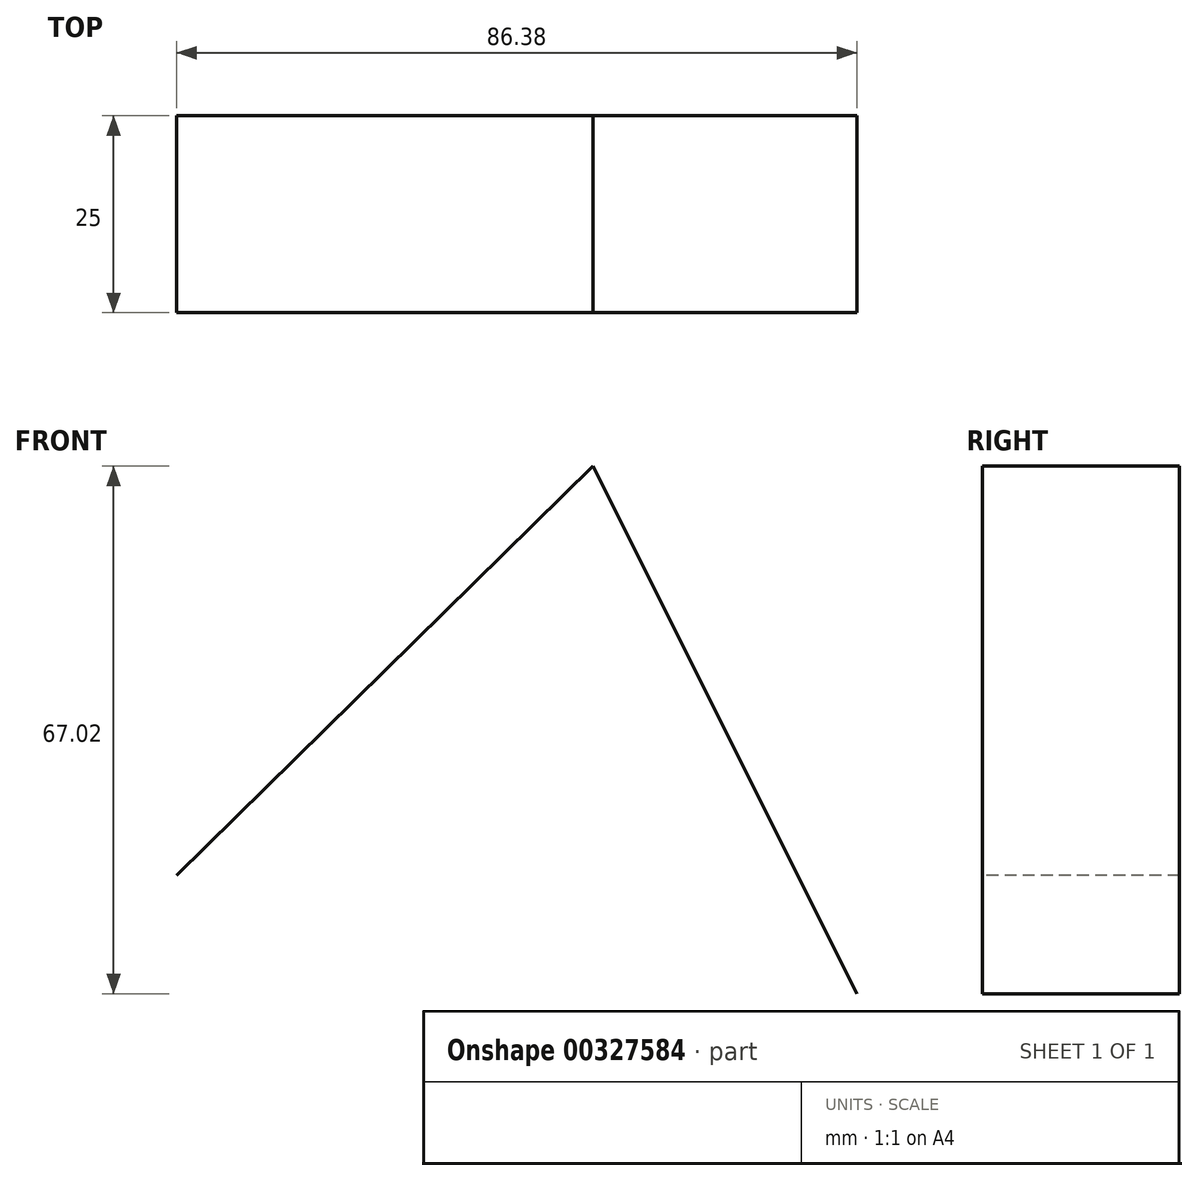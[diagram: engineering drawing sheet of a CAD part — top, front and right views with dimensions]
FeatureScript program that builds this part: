
annotation { "Feature Type Name" : "Feature", "Feature Type Description" : "" }
export const myFeature = defineFeature(function(context is Context, id is Id, definition is map)
    precondition{}
    {
        {
            var Q0;
            Q0=qCreatedBy(makeId("Front.planeOp"),FACE);
            var sketch = newSketch(context, id + "F0", { "sketchPlane" : qUnion([Q0])});
            skLineSegment(sketch, "E0", {"start": v(35.54, 48) * mm, "end": v(88.44, 100.03) * mm});
            skLineSegment(sketch, "E1", {"start": v(88.44, 100.03) * mm, "end": v(121.92, 33) * mm});
            skSolve(sketch);
        }
        {
            var Q0;
            Q0=sQuery(id+"F0.wireOp",EDGE,"E0");
            var Q1;
            Q1=sQuery(id+"F0.wireOp",EDGE,"E1");
            extrude(context, id + "F1", {"bodyType" : ToolBodyType.SURFACE, "surfaceEntities" : qUnion([Q0, Q1]), "depth" : 25 * mm});
        }
    });
